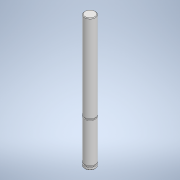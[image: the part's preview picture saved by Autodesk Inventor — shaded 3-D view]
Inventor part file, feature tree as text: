
AUTODESK INVENTOR PART (.ipt)
format: ipt  version: 2022 (Build 260153000, 153)  size: 117,248 bytes
history: native  units: in
note: dims shown in document units (in); Inventor stores cm internally (conversion verified against a paired STEP export)
features: revolve x1, chamfer x1, sketch x1
ambient origin geometry x8: Origin, YZ Plane, XZ Plane, XY Plane, X Axis, Y Axis, Z Axis, Center Point
bodies: Body1 (feature_tree)
feature tree (3):
  revolve  "Revolution1"  [1 undecoded]
  chamfer  "Chamfer1"  Distance=0.0394in
  sketch  "Sketch2"  dims[d3=0.0787in d4=1.9193in d5=0.0394in d6=0.0197in d7=0.0098in d8=0.6299in d9=0.0197in d10=0.0098in d11=90.0deg d12=0.0098in d13=0.125in d14=45.0deg]
note: 1 required parameter value undecoded (feature->parameter linkage not recoverable at this tier; creation-order binding heuristic only, values carry confidence <= 0.55)
